# Revit family: DAL_A3-813X2032-Single-Door-With-Glass-Panel
name_source: partatom
category: Doors
revit_build: Autodesk Revit 2016 (Build: 20150220_1215(x64)
units: mm (PartAtom-declared; Revit-internal decimal feet)

## family parameters
Always vertical = Yes
Cut with Voids When Loaded = No
Host = Wall
Room Calculation Point = No
Shared = No

## types (4) — shared parameters
Frame Size = 110 mm
Frame Width = 44 mm
Function = Interior
Inset = 110 mm
Material Door = Default TIMBER FRAME
Material Frame = Default TIMBER FRAME
PANEL MATERIAL = <By Category>
Panel Width = 40 mm
Wall Closure = By host

## per-type parameters (varying)
| type | Description | Height | Rough Height | Rough Width | Width |
| AC DOORS  A21 813x2032 | STANDARD AC DOORS (A21 813x2032) SOLID 2 PANEL MERANTI  DOOR PANEL AND MERANTI FRAME | 2380 mm  [stored 7.8084 ft] | 2287 mm | 813 mm  [stored 2.66732 ft] | 900 mm |
| AC DOOR A21 762x2032 | STANDARD AC DOORS (A21 762x2032) SOLID 2 PANEL MERANTI  DOOR PANEL AND MERANTI FRAME | 2125 mm | 2032 mm | 763 mm  [stored 2.50328 ft] | 850 mm |
| AC DOORS  A21 813x2032 (FIRE DOOR) | STANDARD AC DOORS (A21 813x2032) SOLID 2 PANEL MERANTI  DOOR PANEL AND MERANTI FRAME | 2125 mm | 2032 mm | 813 mm  [stored 2.66732 ft] | 900 mm |
| AC DOORS  SPECIAL  813x2372 | SPECIAL AC DOORS (A21 813x2372) SOLID 2 PANEL MERANTI  DOOR PANEL AND MERANTI FRAME | 2465 mm | 2372 mm | 813 mm  [stored 2.66732 ft] | 900 mm |

note: [stored X ft] marks values corroborated as IEEE doubles in the binary element streams (Revit-internal decimal feet)

## geometry (parser evidence)
native form markers: Sweep x3
no freeform markers — native parametric forms only
